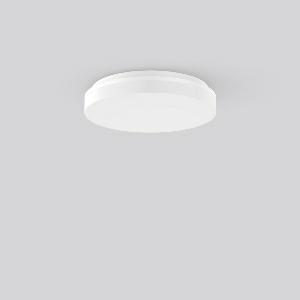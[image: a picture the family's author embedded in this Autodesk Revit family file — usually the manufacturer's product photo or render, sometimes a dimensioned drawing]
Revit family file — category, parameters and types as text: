
# Revit family: hb_505_221187_002_2_2811
name_source: partatom
category: Lighting Fixtures
units: mm (PartAtom-declared; Revit-internal decimal feet)

## family parameters
Cut with Voids When Loaded = No
Host = Face
Light Source = No
Part Type = Normal
Room Calculation Point = No
Round Connector Dimension = Use Diameter
Shared = No

## types (1)
- MultiColor 830 (1 x LED Modul 830, 1600 lm, 3000)
    Apparent Load = 18 VA
    CIE Flux Codes = 43 74 93 91 100
    Color Rendering = 80
    Color Temperature = 3000
    Default Elevation = 1800 mm
    Description = Series: HB 505
Ceiling and wall luminaire with slim design. Housing: plastic (polycarbonate). Diffuser: plastic (polycarbonate), opal. Base and diffuser are sealed together. MultiColour: Colour temperature adjustable via switching element. Choice of 3000 K or 4000 K. Factory setting is 3000 K. Quick mounting adapter galvanized steel sheet, with fastening screws. Driver integrated. 
Colour: white
Diameter: 268 mm
Height: 53 mm
Lamp: LED
Socket: without socket
Colour temperature: 3000K, 4000K
Colour rendering index (CRI): 80
System power: 18 W
Rated luminous flux: 1600 lm
Luminous efficiency: 89 lm/W
System power 2: 18 W
Rated luminous flux 2: 1700 lm
Luminous efficiency 2: 94 lm/W
Control gear: EB
Protection class: I
Type of protection: IP 20
    Height = 53 mm
    Lamp = 1 x LED Modul 830
    Lamp Light Flux = 1600 lm
    Lamp count = 1
    Length = 268 mm
    Lifetime = 50000 h
    Luminous efficacy = 89 lm/W
    Manufacturer = RZB
    ModVariant = No
    Model = 221187.002.2
    Mounting Place = Ceiling, Wall
    Mounting Type = Surface mounted
    Number of Poles = 1
    OnlyDefault = Yes
    Power Factor = 1
    Product Name = HB 505
    Product group = Surface mounted ceiling and wall luminaires
    ProductGroupID = 305
    Protection Class = Protection class I
    Protection Degree = IP 20
    RLX_Detail_Level = 1
    RLX_Emergency_Light_Flux = 0 lm
    RLX_Emergency_Type = 0
    RLX_Emergency_Type_DB = No
    RlxData = <blob elided: 26341 chars, md5=fbfae5a3>
    Socket = socket
    Standby Power = 0 W
    System Light Flux = 1600 lm
    System Power = 18 W
    Type Comments = MultiColor 830
    Type Image = 221187.002.jpg
    URL = http://relux.com
    VarID = multicolor_830
    Voltage = 230 V
    Voltage Range = 220-240 V
    Weight = 0.00 kg
    Width = 0 mm  [stored 0 ft]

note: [stored X ft] marks values corroborated as IEEE doubles in the binary element streams (Revit-internal decimal feet)

## geometry (parser evidence)
native form markers: Blend x4, Sweep x11
no freeform markers — native parametric forms only
